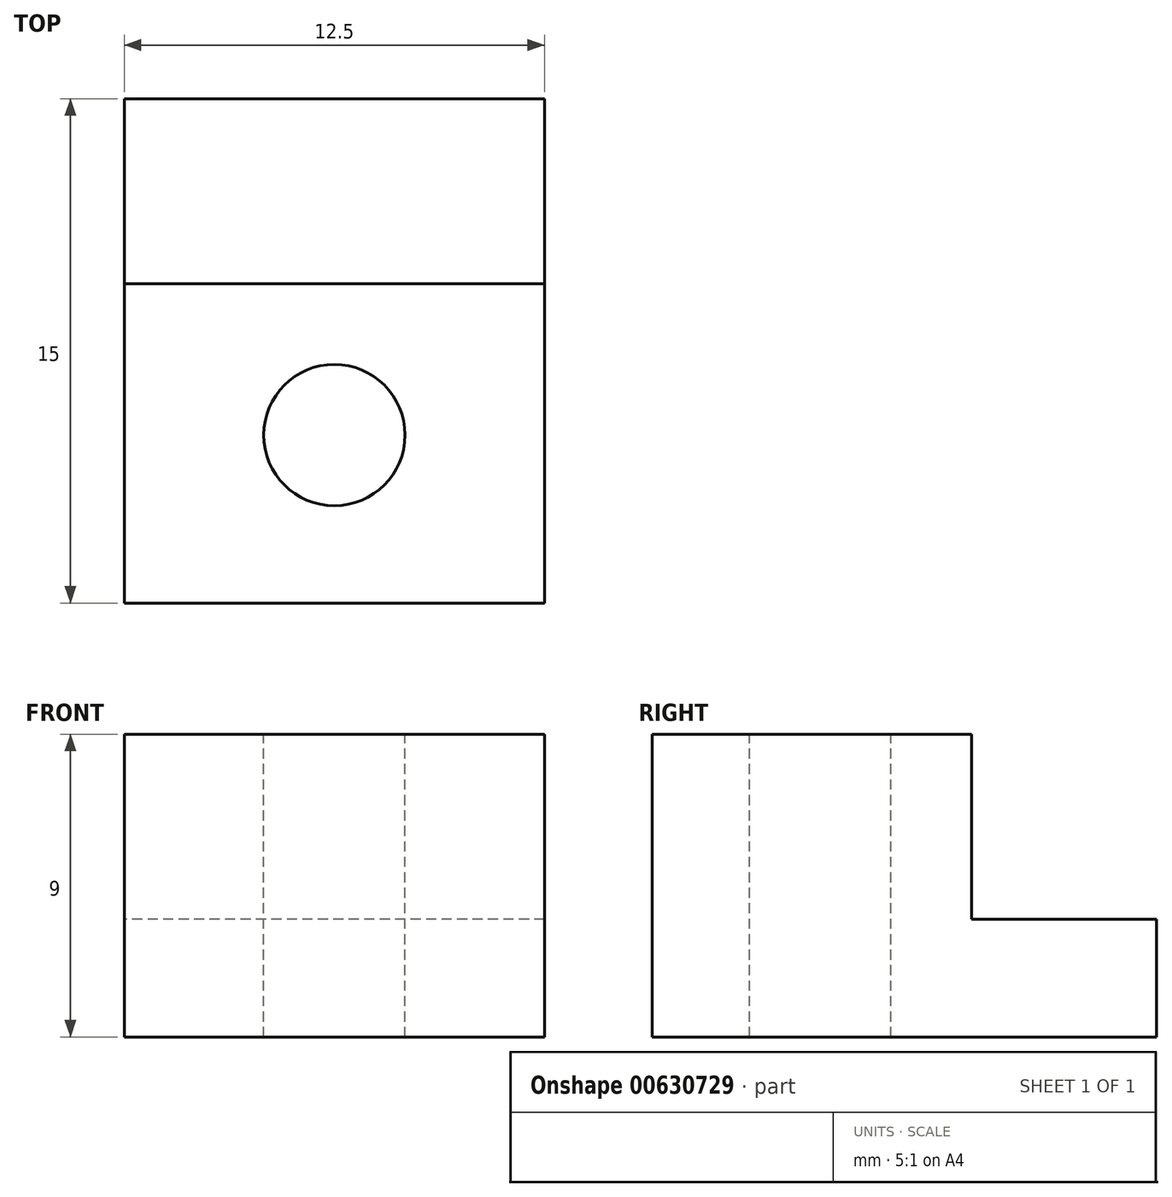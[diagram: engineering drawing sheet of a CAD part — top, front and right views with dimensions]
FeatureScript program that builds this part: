
annotation { "Feature Type Name" : "Feature", "Feature Type Description" : "" }
export const myFeature = defineFeature(function(context is Context, id is Id, definition is map)
    precondition{}
    {
        {
            var Q0;
            Q0=qCreatedBy(makeId("Right.planeOp"),FACE);
            var sketch = newSketch(context, id + "F0", { "sketchPlane" : qUnion([Q0])});
            skLineSegment(sketch, "E0.bottom", {"start": v(-7.63, 1.68) * mm, "end": v(1.87, 1.68) * mm});
            skLineSegment(sketch, "E0.top", {"start": v(-7.63, -7.32) * mm, "end": v(7.37, -7.32) * mm});
            skLineSegment(sketch, "E0.left", {"start": v(-7.63, 1.68) * mm, "end": v(-7.63, -7.32) * mm});
            skLineSegment(sketch, "E0.right", {"start": v(7.37, -3.82) * mm, "end": v(7.37, -7.32) * mm});
            skLineSegment(sketch, "E1.top", {"start": v(1.87, -3.82) * mm, "end": v(7.37, -3.82) * mm});
            skLineSegment(sketch, "E1.left", {"start": v(1.87, 1.68) * mm, "end": v(1.87, -3.82) * mm});
            skSolve(sketch);
        }
        {
            var Q0;
            Q0=makeQuery(id+"F0.imprint","IMPRINT",FACE,{"disambiguationData":[TD([[makeQuery(id+"F0.imprint","IMPRINT",EDGE,{"derivedFrom":sQuery(id+"F0.wireOp",EDGE,"E0.bottom")}),-1.0]])]});
            extrude(context, id + "F1", {"entities" : qUnion([Q0]), "depth" : 12.5 * mm, "offsetDistance" : 25 * mm});
        }
        {
            var Q0;
            Q0=makeQuery(id+"F1.opExtrude","SWEPT_FACE",FACE,{"disambiguationData":[OSD([sQuery(id+"F0.wireOp",EDGE,"E0.bottom")])]});
            var sketch = newSketch(context, id + "F2", { "sketchPlane" : qUnion([Q0])});
            skLineSegment(sketch, "E2", {"start": v(6.25, 1.87) * mm, "end": v(6.25, -7.63) * mm, "construction": true});
            skCircle(sketch, "E3", {"center": v(6.25, -2.63) * mm, "radius": 2.1 * mm});
            skSolve(sketch);
        }
        {
            var Q0;
            Q0=makeQuery(id+"F2.imprint","IMPRINT",FACE,{"disambiguationData":[TD([[makeQuery(id+"F2.imprint","IMPRINT",EDGE,{"derivedFrom":sQuery(id+"F2.wireOp",EDGE,"E3")}),1.0]])]});
            extrude(context, id + "F3", {"entities" : qUnion([Q0]), "operationType" : NewBodyOperationType.REMOVE, "oppositeDirection" : true, "depth" : 25 * mm, "offsetDistance" : 25 * mm});
        }
    });
